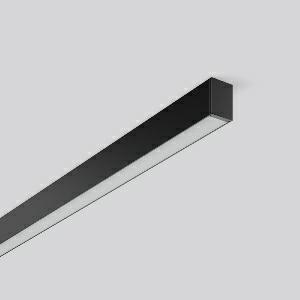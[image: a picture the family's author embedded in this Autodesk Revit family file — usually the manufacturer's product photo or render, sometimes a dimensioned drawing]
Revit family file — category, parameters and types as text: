
# Revit family: less_is_more_27_312199_003_8430
name_source: partatom
category: Lighting Fixtures
units: mm (PartAtom-declared; Revit-internal decimal feet)

## family parameters
Cut with Voids When Loaded = No
Host = Face
Light Source = No
Part Type = Normal
Room Calculation Point = No
Round Connector Dimension = Use Diameter
Shared = No

## types (1)
- LESS IS MORE 27 (1 x LED Modul 830, 2200 lm, 3000)
    Apparent Load = 34 VA
    CIE Flux Codes = 65 89 98 100 100
    Color Rendering = 80
    Color Temperature = 3000
    Default Elevation = 1800 mm
    Description = Series: LESS IS MORE 27
Ceiling luminaire with slim design. Housing: extruded aluminium profile, powder-coated. End cap aluminium powder-coated. Diffuser made of non-yellowing plastic (PMMA) microprismatic. Suitable for Ceiling mounting, Wall (surface). External driver with connecting cable. 
Colour: deep black, matt (RAL 9005)
Length: 1212 mm
Width: 28 mm
Height: 38 mm
Lamp: LED
Socket: without socket
Colour temperature: 3000K
Colour rendering index (CRI): 82
System power: 34 W
Rated luminous flux: 2200 lm
Luminous efficiency: 65 lm/W
Control gear: Regulated power supply
Protection class: II
Type of protection: IP 20
    Height = 38 mm
    Lamp = 1 x LED Modul 830
    Lamp Light Flux = 2200 lm
    Lamp count = 1
    Length = 1212 mm
    Lifetime = 50000 h
    Luminous efficacy = 65 lm/W
    Manufacturer = RZB
    ModVariant = No
    Model = 312199.003
    Mounting Place = Wall, Ceiling
    Mounting Type = Surface mounted
    Number of Poles = 1
    OnlyDefault = Yes
    Power Factor = 1
    Product Name = LESS IS MORE 27
    Product group = Surface mounted LED linear luminaires
    ProductGroupID = 307
    Protection Class = Protection class II
    Protection Degree = IP 20
    RLX_Detail_Level = 1
    RLX_Emergency_Light_Flux = 0 lm
    RLX_Emergency_Type = 0
    RLX_Emergency_Type_DB = No
    RlxData = <blob elided: 29773 chars, md5=0496680c>
    Socket = socket
    Standby Power = 0 W
    System Light Flux = 2200 lm
    System Power = 34 W
    Type Comments = Product without accessories
    Type Image = 312197.003.jpg
    URL = http://relux.com
    VarID = ---
    Voltage = 230 V
    Voltage Range = 220-240 V
    Weight = 0.00 kg
    Width = 28 mm

## geometry (parser evidence)
native form markers: Blend x4, Sweep x9
no freeform markers — native parametric forms only
